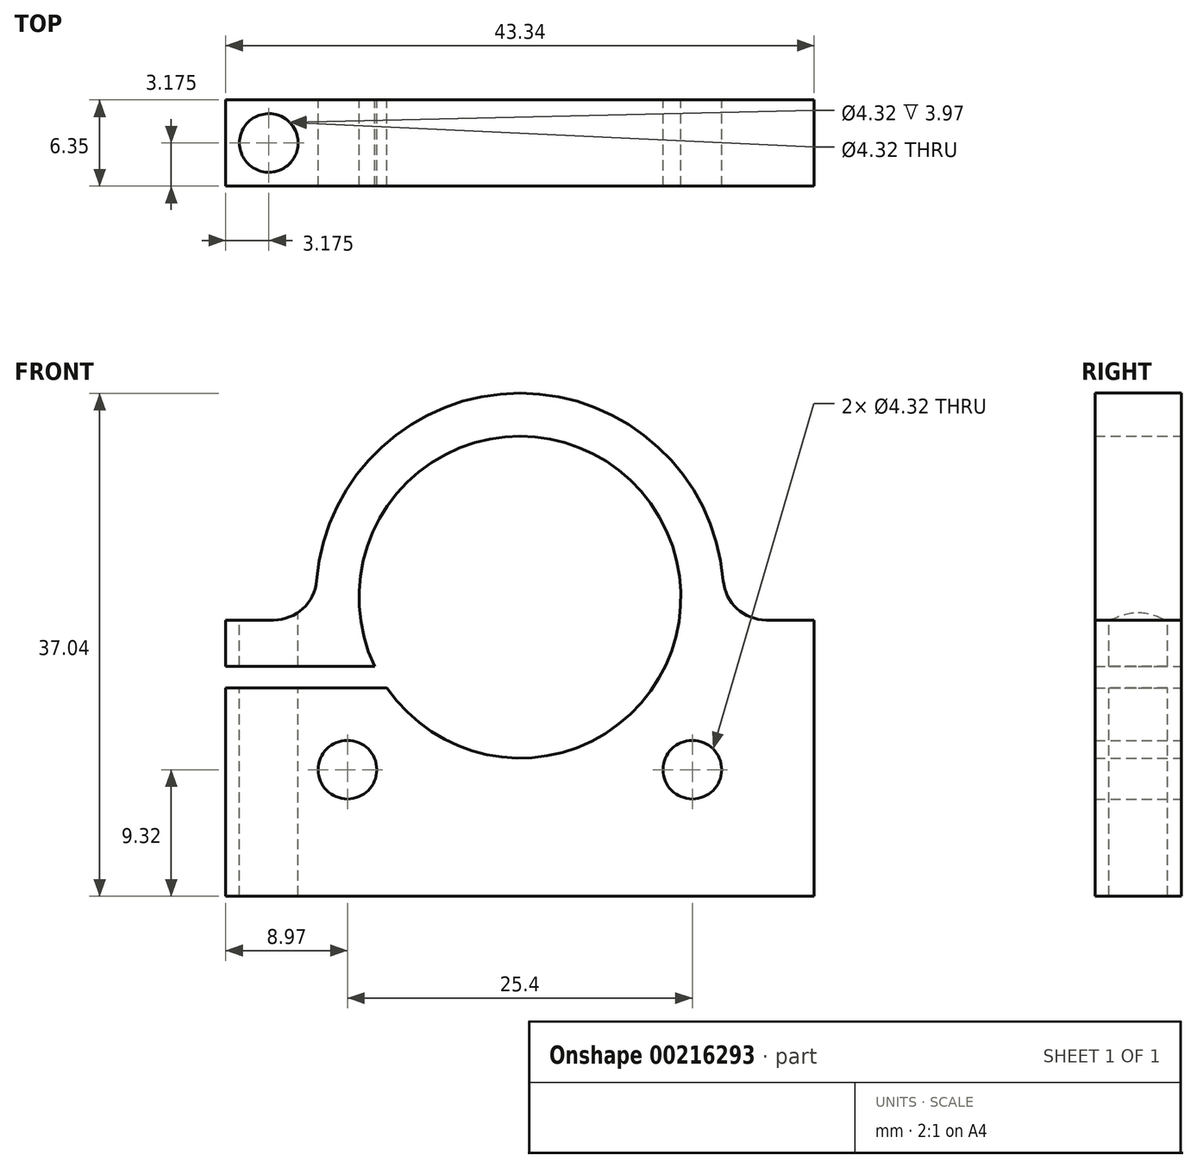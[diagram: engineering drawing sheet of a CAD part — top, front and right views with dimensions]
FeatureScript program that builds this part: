
annotation { "Feature Type Name" : "Feature", "Feature Type Description" : "" }
export const myFeature = defineFeature(function(context is Context, id is Id, definition is map)
    precondition{}
    {
        {
            var Q0;
            Q0=qCreatedBy(makeId("Front.planeOp"),FACE);
            var sketch = newSketch(context, id + "F0", { "sketchPlane" : qUnion([Q0])});
            skArc(sketch, "E0", {"start": v(-9.79, -6.68) * mm, "mid": v(10.28, 5.9) * mm, "end": v(-10.7, -5.09) * mm});
            skArc(sketch, "E1", {"start": v(14.97, 1.23) * mm, "mid": v(0, 15.02) * mm, "end": v(-14.97, 1.23) * mm});
            skLineSegment(sketch, "E2.bottom", {"start": v(-21.67, -1.68) * mm, "end": v(-18.14, -1.68) * mm});
            skLineSegment(sketch, "E2.top", {"start": v(-21.67, -22.02) * mm, "end": v(21.67, -22.02) * mm});
            skLineSegment(sketch, "E2.left", {"start": v(-21.67, -1.68) * mm, "end": v(-21.67, -5.09) * mm});
            skLineSegment(sketch, "E2.right", {"start": v(21.67, -1.68) * mm, "end": v(21.67, -22.02) * mm});
            skPoint(sketch, "E2.middle", {"position": v(0, -11.85) * mm});
            skLineSegment(sketch, "E3", {"start": v(-21.67, -5.09) * mm, "end": v(-10.7, -5.09) * mm});
            skLineSegment(sketch, "E4", {"start": v(-21.67, -6.68) * mm, "end": v(-9.79, -6.68) * mm});
            skLineSegment(sketch, "E5.trimOffspring", {"start": v(-21.67, -6.68) * mm, "end": v(-21.67, -22.02) * mm});
            skLineSegment(sketch, "E6.trimOffspring", {"start": v(18.14, -1.68) * mm, "end": v(21.67, -1.68) * mm});
            skPoint(sketch, "E7.visualSharp", {"position": v(-14.93, -1.68) * mm});
            skArc(sketch, "E7.filletArc", {"start": v(-18.14, -1.68) * mm, "mid": v(-15.99, -0.84) * mm, "end": v(-14.97, 1.23) * mm});
            skPoint(sketch, "E8.visualSharp", {"position": v(14.93, -1.68) * mm});
            skArc(sketch, "E8.filletArc", {"start": v(14.97, 1.23) * mm, "mid": v(15.99, -0.84) * mm, "end": v(18.14, -1.68) * mm});
            skLineSegment(sketch, "E9", {"start": v(-21.67, -12.7) * mm, "end": v(21.67, -12.7) * mm, "construction": true});
            skLineSegment(sketch, "E10", {"start": v(-12.7, -6.68) * mm, "end": v(-12.7, -22.02) * mm, "construction": true});
            skCircle(sketch, "E11", {"center": v(-12.7, -12.7) * mm, "radius": 2.16 * mm});
            skPoint(sketch, "E12", {"position": v(-12.7, -14.35) * mm});
            skCircle(sketch, "E13.MirrorC", {"center": v(12.7, -12.7) * mm, "radius": 2.16 * mm});
            skSolve(sketch);
        }
        {
            var Q0;
            Q0=qSketchRegion(id+"F0",true);
            extrude(context, id + "F1", {"entities" : qUnion([Q0]), "depth" : 6.35 * mm});
        }
        {
            var Q0;
            Q0=makeQuery(id+"F1.opExtrude","SWEPT_FACE",FACE,{"disambiguationData":[OSD([sQuery(id+"F0.wireOp",EDGE,"E2.bottom")])]});
            var sketch = newSketch(context, id + "F2", { "sketchPlane" : qUnion([Q0])});
            skLineSegment(sketch, "E14", {"start": v(-21.67, -3.18) * mm, "end": v(21.64, -3.18) * mm, "construction": true});
            skPoint(sketch, "E14.endSnap0", {"position": v(-21.67, -3.18) * mm});
            skCircle(sketch, "E15", {"center": v(-18.5, -3.18) * mm, "radius": 2.16 * mm});
            skSolve(sketch);
        }
        {
            var Q0;
            Q0=qSketchRegion(id+"F2",true);
            extrude(context, id + "F3", {"entities" : qUnion([Q0]), "operationType" : NewBodyOperationType.REMOVE, "endBound" : BoundingType.SYMMETRIC, "oppositeDirection" : true, "depth" : 76.2 * mm});
        }
    });
